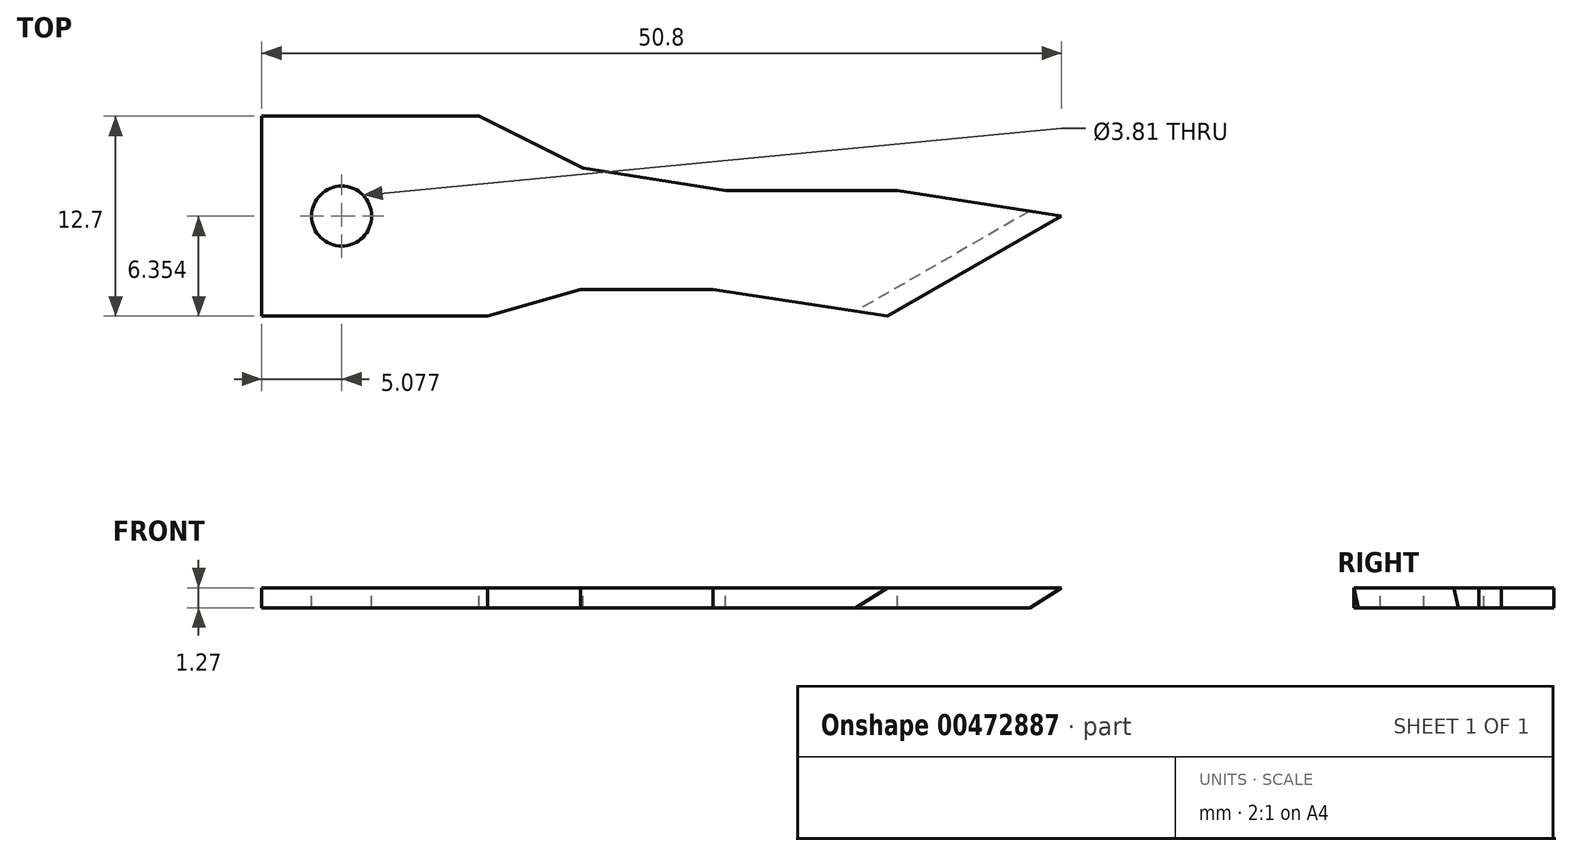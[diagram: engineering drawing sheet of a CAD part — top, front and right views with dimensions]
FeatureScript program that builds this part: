
annotation { "Feature Type Name" : "Feature", "Feature Type Description" : "" }
export const myFeature = defineFeature(function(context is Context, id is Id, definition is map)
    precondition{}
    {
        {
            var Q0;
            Q0=qCreatedBy(makeId("Top.planeOp"),FACE);
            var sketch = newSketch(context, id + "F0", { "sketchPlane" : qUnion([Q0])});
            skLineSegment(sketch, "E0.bottom", {"start": v(18.06, -27.4) * mm, "end": v(68.86, -27.4) * mm});
            skLineSegment(sketch, "E0.top", {"start": v(18.06, -14.7) * mm, "end": v(68.86, -14.7) * mm});
            skLineSegment(sketch, "E0.left", {"start": v(18.06, -27.4) * mm, "end": v(18.06, -14.7) * mm});
            skLineSegment(sketch, "E0.right", {"start": v(68.86, -27.4) * mm, "end": v(68.86, -14.7) * mm});
            skSolve(sketch);
        }
        {
            var Q0;
            Q0=makeQuery(id+"F0.imprint","IMPRINT",FACE,{"disambiguationData":[TD([[makeQuery(id+"F0.imprint","IMPRINT",EDGE,{"derivedFrom":sQuery(id+"F0.wireOp",EDGE,"E0.bottom")}),1.0]])]});
            extrude(context, id + "F1", {"entities" : qUnion([Q0]), "depth" : 1.27 * mm});
        }
        {
            var Q0;
            Q0=makeQuery(id+"F1.opExtrude","CAP_FACE",FACE,{"disambiguationData":[OSD([sQuery(id+"F0.wireOp",EDGE,"E0.bottom"),sQuery(id+"F0.wireOp",EDGE,"E0.top"),sQuery(id+"F0.wireOp",EDGE,"E0.left"),sQuery(id+"F0.wireOp",EDGE,"E0.right")])],"isStart":false});
            var sketch = newSketch(context, id + "F2", { "sketchPlane" : qUnion([Q0])});
            skCircle(sketch, "E1", {"center": v(23.14, -21.06) * mm, "radius": 1.9 * mm});
            skSolve(sketch);
        }
        {
            var Q0;
            Q0=makeQuery(id+"F2.imprint","IMPRINT",FACE,{"disambiguationData":[TD([[makeQuery(id+"F2.imprint","IMPRINT",EDGE,{"derivedFrom":sQuery(id+"F2.wireOp",EDGE,"E1")}),1.0]])]});
            extrude(context, id + "F3", {"entities" : qUnion([Q0]), "operationType" : NewBodyOperationType.REMOVE, "oppositeDirection" : true, "depth" : 25.4 * mm});
        }
        {
            var Q0;
            Q0=makeQuery(id+"F1.opExtrude","CAP_FACE",FACE,{"disambiguationData":[OSD([sQuery(id+"F0.wireOp",EDGE,"E0.bottom"),sQuery(id+"F0.wireOp",EDGE,"E0.top"),sQuery(id+"F0.wireOp",EDGE,"E0.left"),sQuery(id+"F0.wireOp",EDGE,"E0.right")])],"isStart":false});
            var sketch = newSketch(context, id + "F4", { "sketchPlane" : qUnion([Q0])});
            skLineSegment(sketch, "E2", {"start": v(68.86, -21.06) * mm, "end": v(57.8, -27.4) * mm});
            skLineSegment(sketch, "E3", {"start": v(57.8, -27.4) * mm, "end": v(46.7, -25.7) * mm});
            skLineSegment(sketch, "E4", {"start": v(46.7, -25.7) * mm, "end": v(38.3, -25.7) * mm});
            skLineSegment(sketch, "E5", {"start": v(38.3, -25.7) * mm, "end": v(32.4, -27.4) * mm});
            skLineSegment(sketch, "E6", {"start": v(68.86, -21.06) * mm, "end": v(58.42, -19.45) * mm});
            skLineSegment(sketch, "E7", {"start": v(58.42, -19.45) * mm, "end": v(47.51, -19.45) * mm});
            skLineSegment(sketch, "E8", {"start": v(47.51, -19.45) * mm, "end": v(38.48, -18.02) * mm});
            skLineSegment(sketch, "E9", {"start": v(38.48, -18.02) * mm, "end": v(31.86, -14.7) * mm});
            skSolve(sketch);
        }
        {
            var Q0;
            {var subQ4=sQuery(id+"F4.wireOp",EDGE,"E6");Q0=makeQuery(id+"F4.imprint","IMPRINT",FACE,{"disambiguationData":[TD([[makeQuery(id+"F4.imprint","IMPRINT",EDGE,{"derivedFrom":subQ4}),-1.0]])]});}
            var Q1;
            {var subQ0=sQuery(id+"F4.wireOp",EDGE,"E2");Q1=makeQuery(id+"F4.imprint","IMPRINT",FACE,{"disambiguationData":[TD([[makeQuery(id+"F4.imprint","IMPRINT",EDGE,{"derivedFrom":subQ0}),1.0]])]});}
            var Q2;
            {var subQ0=sQuery(id+"F4.wireOp",EDGE,"E3");Q2=makeQuery(id+"F4.imprint","IMPRINT",FACE,{"disambiguationData":[TD([[makeQuery(id+"F4.imprint","IMPRINT",EDGE,{"derivedFrom":subQ0}),1.0]])]});}
            extrude(context, id + "F5", {"entities" : qUnion([Q0, Q1, Q2]), "operationType" : NewBodyOperationType.REMOVE, "oppositeDirection" : true, "depth" : 25.4 * mm});
        }
        {
            var Q0;
            Q0=makeQuery(id+"F5.boolean.opBoolean","COPY",EDGE,{"derivedFrom":makeQuery(id+"F5.opExtrude","CAP_EDGE",EDGE,{"disambiguationData":[OSD([sQuery(id+"F4.wireOp",EDGE,"E2")])],"isStart":true})});
            var Q1;
            Q1=makeQuery(id+"F5.boolean.opBoolean","INTERSECT",EDGE,{"derivedFrom":[makeQuery(id+"F1.opExtrude","CAP_FACE",FACE,{"disambiguationData":[OSD([sQuery(id+"F0.wireOp",EDGE,"E0.bottom"),sQuery(id+"F0.wireOp",EDGE,"E0.top"),sQuery(id+"F0.wireOp",EDGE,"E0.left"),sQuery(id+"F0.wireOp",EDGE,"E0.right")])],"isStart":true}),makeQuery(id+"F5.opExtrude","SWEPT_FACE",FACE,{"disambiguationData":[OSD([sQuery(id+"F4.wireOp",EDGE,"E2")])]})]});
            chamfer(context, id + "F6", {"entities" : qUnion([Q0, Q1]), "width" : 1.27 * mm, "tangentPropagation" : true});
        }
    });
